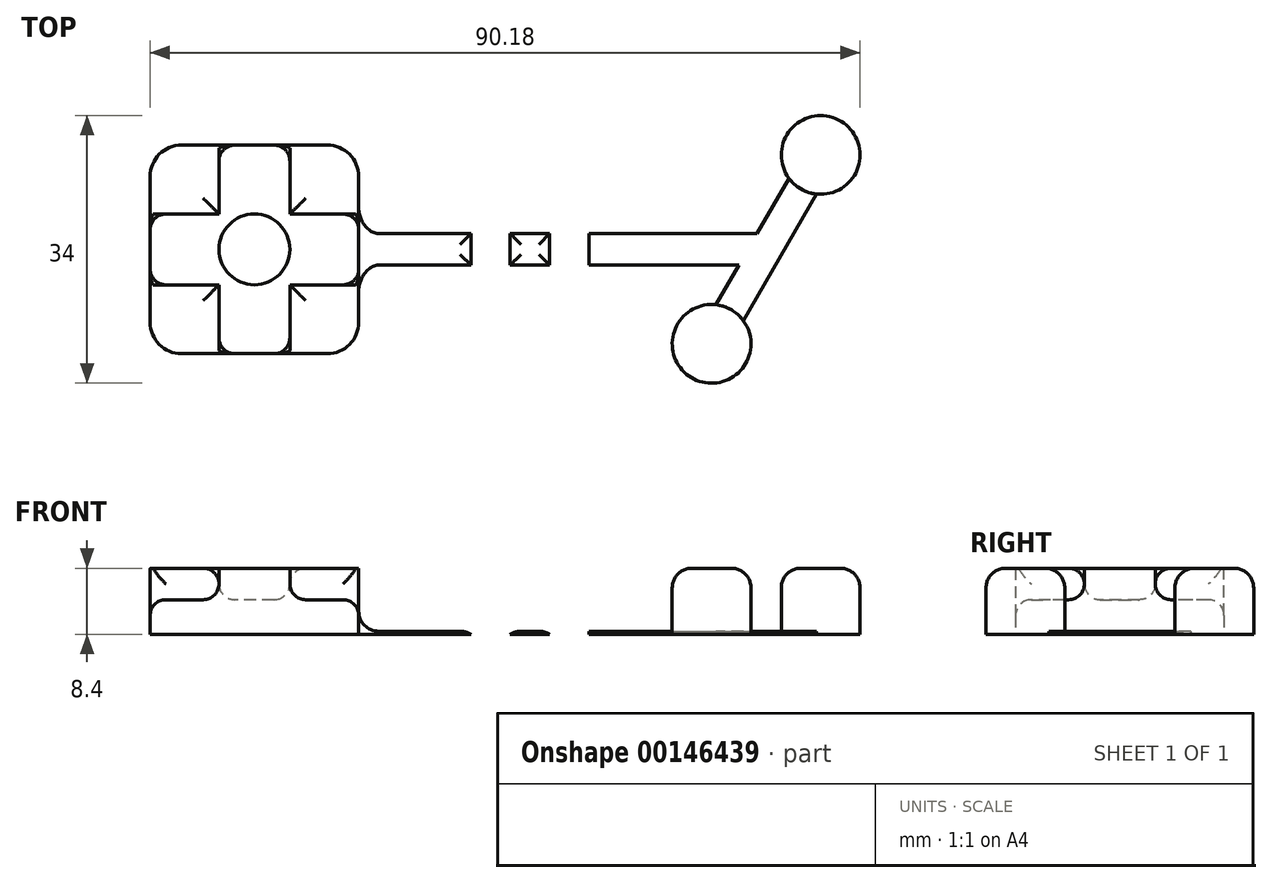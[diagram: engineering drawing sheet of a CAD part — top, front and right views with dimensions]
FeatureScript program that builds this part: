
annotation { "Feature Type Name" : "Feature", "Feature Type Description" : "" }
export const myFeature = defineFeature(function(context is Context, id is Id, definition is map)
    precondition{}
    {
        {
            var Q0;
            Q0=qCreatedBy(makeId("Top.planeOp"),FACE);
            var sketch = newSketch(context, id + "F0", { "sketchPlane" : qUnion([Q0])});
            skLineSegment(sketch, "E0.bottom", {"start": v(13.25, 13.25) * mm, "end": v(-13.25, 13.25) * mm});
            skLineSegment(sketch, "E0.top", {"start": v(13.25, -13.25) * mm, "end": v(-13.25, -13.25) * mm});
            skLineSegment(sketch, "E0.left", {"start": v(13.25, 13.25) * mm, "end": v(13.25, -13.25) * mm});
            skLineSegment(sketch, "E0.right", {"start": v(-13.25, 13.25) * mm, "end": v(-13.25, -13.25) * mm});
            skPoint(sketch, "E0.middle", {"position": v(0, 0) * mm});
            skLineSegment(sketch, "E1", {"start": v(0, 0) * mm, "end": v(65, 0) * mm, "construction": true});
            skLineSegment(sketch, "E2", {"start": v(60.57, -7.67) * mm, "end": v(71.93, 12) * mm, "construction": true});
            skPoint(sketch, "E3", {"position": v(58.07, -12) * mm});
            skCircle(sketch, "E4", {"center": v(71.93, 12) * mm, "radius": 5 * mm});
            skCircle(sketch, "E5", {"center": v(58.07, -12) * mm, "radius": 5 * mm});
            skLineSegment(sketch, "E6.bottom", {"start": v(32.5, 3) * mm, "end": v(27.5, 3) * mm, "construction": true});
            skLineSegment(sketch, "E6.top", {"start": v(32.5, -3) * mm, "end": v(27.5, -3) * mm, "construction": true});
            skLineSegment(sketch, "E6.left", {"start": v(32.5, 3) * mm, "end": v(32.5, -3) * mm});
            skLineSegment(sketch, "E6.right", {"start": v(27.5, 3) * mm, "end": v(27.5, -3) * mm});
            skPoint(sketch, "E6.middle", {"position": v(30, 0) * mm});
            skPoint(sketch, "E7.middle", {"position": v(32.5, 0) * mm});
            skLineSegment(sketch, "E8.bottom", {"start": v(42.5, 3) * mm, "end": v(37.5, 3) * mm, "construction": true});
            skLineSegment(sketch, "E8.top", {"start": v(42.5, -3) * mm, "end": v(37.5, -3) * mm, "construction": true});
            skLineSegment(sketch, "E8.left", {"start": v(42.5, 3) * mm, "end": v(42.5, -3) * mm});
            skLineSegment(sketch, "E8.right", {"start": v(37.5, 3) * mm, "end": v(37.5, -3) * mm});
            skPoint(sketch, "E8.middle", {"position": v(40, 0) * mm});
            skArc(sketch, "E9", {"start": v(37.5, 3) * mm, "mid": v(40, 5.5) * mm, "end": v(42.5, 3) * mm});
            skArc(sketch, "E10", {"start": v(42.5, -3) * mm, "mid": v(40, -5.5) * mm, "end": v(37.5, -3) * mm});
            skArc(sketch, "E11", {"start": v(27.5, 3) * mm, "mid": v(30, 5.5) * mm, "end": v(32.5, 3) * mm});
            skArc(sketch, "E12", {"start": v(32.5, -3) * mm, "mid": v(30, -5.5) * mm, "end": v(27.5, -3) * mm});
            skLineSegment(sketch, "E13.0", {"start": v(58.63, -7.03) * mm, "end": v(67.9, 9.03) * mm});
            skLineSegment(sketch, "E14.MirrorCS", {"start": v(62.1, -9.03) * mm, "end": v(71.37, 7.03) * mm});
            skLineSegment(sketch, "E15", {"start": v(13.25, 2) * mm, "end": v(27.5, 2) * mm});
            skLineSegment(sketch, "E16", {"start": v(32.5, 2) * mm, "end": v(37.5, 2) * mm});
            skLineSegment(sketch, "E17", {"start": v(42.5, 2) * mm, "end": v(63.85, 2) * mm});
            skLineSegment(sketch, "E18.MirrorCS", {"start": v(13.25, -2) * mm, "end": v(27.5, -2) * mm});
            skLineSegment(sketch, "E19.MirrorCS", {"start": v(32.5, -2) * mm, "end": v(37.5, -2) * mm});
            skLineSegment(sketch, "E20.MirrorCS", {"start": v(42.5, -2) * mm, "end": v(63.85, -2) * mm});
            skSolve(sketch);
        }
        {
            var Q0;
            {var subQ3=sQuery(id+"F0.wireOp",EDGE,"E0.bottom");Q0=makeQuery(id+"F0.imprint","IMPRINT",FACE,{"disambiguationData":[TD([[makeQuery(id+"F0.imprint","IMPRINT",EDGE,{"derivedFrom":subQ3}),1.0]])]});}
            var Q1;
            {var subQ0=sQuery(id+"F0.wireOp",EDGE,"E11");Q1=makeQuery(id+"F0.imprint","IMPRINT",FACE,{"disambiguationData":[TD([[makeQuery(id+"F0.imprint","IMPRINT",EDGE,{"derivedFrom":subQ0}),-1.0]])]});}
            var Q2;
            {var subQ0=sQuery(id+"F0.wireOp",EDGE,"E9");Q2=makeQuery(id+"F0.imprint","IMPRINT",FACE,{"disambiguationData":[TD([[makeQuery(id+"F0.imprint","IMPRINT",EDGE,{"derivedFrom":subQ0}),-1.0]])]});}
            var Q3;
            {var subQ0=sQuery(id+"F0.wireOp",EDGE,"E4");var subQ1=makeQuery(id+"F0.imprint","INTERSECT",VERTEX,{"derivedFrom":[subQ0,sQuery(id+"F0.wireOp",EDGE,"E13.0")]});Q3=makeQuery(id+"F0.imprint","IMPRINT",FACE,{"disambiguationData":[TD([[makeQuery(id+"F0.imprint","IMPRINT",EDGE,{"disambiguationData":[TD([[subQ1,-1.0]])],"derivedFrom":subQ0}),1.0]])]});}
            var Q4;
            {var subQ0=sQuery(id+"F0.wireOp",EDGE,"E5");var subQ1=makeQuery(id+"F0.imprint","INTERSECT",VERTEX,{"derivedFrom":[subQ0,sQuery(id+"F0.wireOp",EDGE,"E13.0")]});Q4=makeQuery(id+"F0.imprint","IMPRINT",FACE,{"disambiguationData":[TD([[makeQuery(id+"F0.imprint","IMPRINT",EDGE,{"disambiguationData":[TD([[subQ1,1.0]])],"derivedFrom":subQ0}),1.0]])]});}
            extrude(context, id + "F1", {"entities" : qUnion([Q0, Q1, Q2, Q3, Q4]), "depth" : 8 * mm});
        }
        {
            var Q0;
            {var subQ0=sQuery(id+"F0.wireOp",EDGE,"E15");Q0=makeQuery(id+"F0.imprint","IMPRINT",FACE,{"disambiguationData":[TD([[makeQuery(id+"F0.imprint","IMPRINT",EDGE,{"derivedFrom":subQ0}),-1.0]])]});}
            var Q1;
            {var subQ0=sQuery(id+"F0.wireOp",EDGE,"E16");Q1=makeQuery(id+"F0.imprint","IMPRINT",FACE,{"disambiguationData":[TD([[makeQuery(id+"F0.imprint","IMPRINT",EDGE,{"derivedFrom":subQ0}),-1.0]])]});}
            var Q2;
            {var subQ0=sQuery(id+"F0.wireOp",EDGE,"E17");Q2=makeQuery(id+"F0.imprint","IMPRINT",FACE,{"disambiguationData":[TD([[makeQuery(id+"F0.imprint","IMPRINT",EDGE,{"derivedFrom":subQ0}),-1.0]])]});}
            var Q3;
            {var subQ5=sQuery(id+"F0.wireOp",EDGE,"E14.MirrorCS");Q3=makeQuery(id+"F0.imprint","IMPRINT",FACE,{"disambiguationData":[TD([[makeQuery(id+"F0.imprint","IMPRINT",EDGE,{"derivedFrom":subQ5}),1.0]])]});}
            var Q4;
            Q4=makeQuery(id+"F1.opExtrude","CAP_FACE",FACE,{"disambiguationData":[OSD([sQuery(id+"F0.wireOp",EDGE,"E0.bottom"),sQuery(id+"F0.wireOp",EDGE,"E0.top"),sQuery(id+"F0.wireOp",EDGE,"E0.left"),sQuery(id+"F0.wireOp",EDGE,"E0.right")])],"isStart":false});
            var Q5;
            Q5=makeQuery(id+"F1.opExtrude","CAP_FACE",FACE,{"disambiguationData":[OSD([sQuery(id+"F0.wireOp",EDGE,"E6.left"),sQuery(id+"F0.wireOp",EDGE,"E6.right"),sQuery(id+"F0.wireOp",EDGE,"E11"),sQuery(id+"F0.wireOp",EDGE,"E12")])],"isStart":false});
            var Q6;
            Q6=makeQuery(id+"F1.opExtrude","CAP_FACE",FACE,{"disambiguationData":[OSD([sQuery(id+"F0.wireOp",EDGE,"E8.left"),sQuery(id+"F0.wireOp",EDGE,"E8.right"),sQuery(id+"F0.wireOp",EDGE,"E9"),sQuery(id+"F0.wireOp",EDGE,"E10")])],"isStart":false});
            var Q7;
            Q7=makeQuery(id+"F1.opExtrude","CAP_FACE",FACE,{"disambiguationData":[OSD([sQuery(id+"F0.wireOp",EDGE,"E5")])],"isStart":false});
            var Q8;
            Q8=makeQuery(id+"F1.opExtrude","CAP_FACE",FACE,{"disambiguationData":[OSD([sQuery(id+"F0.wireOp",EDGE,"E4")])],"isStart":false});
            extrude(context, id + "F2", {"entities" : qUnion([Q0, Q1, Q2, Q3, Q4, Q5, Q6, Q7, Q8]), "operationType" : NewBodyOperationType.ADD, "depth" : 0.4 * mm});
        }
        {
            var Q0;
            Q0=makeQuery(id+"F2.opExtrude","CAP_FACE",FACE,{"disambiguationData":[OSD([sQuery(id+"F0.wireOp",EDGE,"E4")])],"isStart":false});
            var Q1;
            Q1=makeQuery(id+"F2.opExtrude","CAP_FACE",FACE,{"disambiguationData":[OSD([sQuery(id+"F0.wireOp",EDGE,"E5")])],"isStart":false});
            var Q2;
            Q2=makeQuery(id+"F2.opExtrude","CAP_FACE",FACE,{"disambiguationData":[OSD([sQuery(id+"F0.wireOp",EDGE,"E8.left"),sQuery(id+"F0.wireOp",EDGE,"E8.right"),sQuery(id+"F0.wireOp",EDGE,"E9"),sQuery(id+"F0.wireOp",EDGE,"E10")])],"isStart":false});
            var Q3;
            Q3=makeQuery(id+"F2.opExtrude","CAP_FACE",FACE,{"disambiguationData":[OSD([sQuery(id+"F0.wireOp",EDGE,"E6.left"),sQuery(id+"F0.wireOp",EDGE,"E6.right"),sQuery(id+"F0.wireOp",EDGE,"E11"),sQuery(id+"F0.wireOp",EDGE,"E12")])],"isStart":false});
            fillet(context, id + "F3", {"entities" : qUnion([Q0, Q1, Q2, Q3]), "radius" : 2.5 * mm, "tangentPropagation" : true, "allowEdgeOverflow" : false});
        }
        {
            var Q0;
            Q0=makeQuery(id+"F2.opExtrude","CAP_FACE",FACE,{"disambiguationData":[OSD([sQuery(id+"F0.wireOp",EDGE,"E0.bottom"),sQuery(id+"F0.wireOp",EDGE,"E0.top"),sQuery(id+"F0.wireOp",EDGE,"E0.left"),sQuery(id+"F0.wireOp",EDGE,"E0.right")])],"isStart":false});
            var sketch = newSketch(context, id + "F4", { "sketchPlane" : qUnion([Q0])});
            skCircle(sketch, "E21", {"center": v(0, 0) * mm, "radius": 4.5 * mm});
            skLineSegment(sketch, "E22", {"start": v(-4.5, 13.25) * mm, "end": v(-4.5, 4.5) * mm});
            skLineSegment(sketch, "E23", {"start": v(-13.25, 4.5) * mm, "end": v(-4.5, 4.5) * mm});
            skLineSegment(sketch, "E24", {"start": v(4.5, 13.25) * mm, "end": v(4.5, 4.5) * mm});
            skLineSegment(sketch, "E25", {"start": v(-13.86, -4.5) * mm, "end": v(-4.5, -4.5) * mm});
            skLineSegment(sketch, "E26.trimOffspring", {"start": v(4.5, 4.5) * mm, "end": v(13.25, 4.5) * mm});
            skLineSegment(sketch, "E27.trimOffspring", {"start": v(4.5, -4.5) * mm, "end": v(13.25, -4.5) * mm});
            skLineSegment(sketch, "E28.trimOffspring", {"start": v(-4.5, -4.5) * mm, "end": v(-4.5, -13.25) * mm});
            skLineSegment(sketch, "E29.trimOffspring", {"start": v(4.5, -4.5) * mm, "end": v(4.5, -13.25) * mm});
            skSolve(sketch);
        }
        {
            var Q0;
            {var subQ0=sQuery(id+"F4.wireOp",EDGE,"E24");Q0=makeQuery(id+"F4.imprint","IMPRINT",FACE,{"disambiguationData":[TD([[makeQuery(id+"F4.imprint","IMPRINT",EDGE,{"derivedFrom":subQ0}),1.0]])]});}
            var Q1;
            {var subQ0=sQuery(id+"F4.wireOp",EDGE,"E22");Q1=makeQuery(id+"F4.imprint","IMPRINT",FACE,{"disambiguationData":[TD([[makeQuery(id+"F4.imprint","IMPRINT",EDGE,{"derivedFrom":subQ0}),-1.0]])]});}
            var Q2;
            {var subQ0=sQuery(id+"F4.wireOp",EDGE,"E28.trimOffspring");Q2=makeQuery(id+"F4.imprint","IMPRINT",FACE,{"disambiguationData":[TD([[makeQuery(id+"F4.imprint","IMPRINT",EDGE,{"derivedFrom":subQ0}),-1.0]])]});}
            var Q3;
            {var subQ0=sQuery(id+"F4.wireOp",EDGE,"E27.trimOffspring");Q3=makeQuery(id+"F4.imprint","IMPRINT",FACE,{"disambiguationData":[TD([[makeQuery(id+"F4.imprint","IMPRINT",EDGE,{"derivedFrom":subQ0}),-1.0]])]});}
            var Q4;
            Q4=makeQuery(id+"F4.imprint","IMPRINT",FACE,{"disambiguationData":[TD([[makeQuery(id+"F4.imprint","IMPRINT",EDGE,{"derivedFrom":sQuery(id+"F4.wireOp",EDGE,"E21")}),1.0]])]});
            extrude(context, id + "F5", {"entities" : qUnion([Q0, Q1, Q2, Q3, Q4]), "operationType" : NewBodyOperationType.REMOVE, "oppositeDirection" : true, "depth" : 4 * mm});
        }
        {
            var Q0;
            Q0=makeQuery(id+"F5.boolean.opBoolean","COPY",FACE,{"derivedFrom":makeQuery(id+"F5.opExtrude","CAP_FACE",FACE,{"disambiguationData":[OSD([sQuery(id+"F0.wireOp",EDGE,"E0.top"),sQuery(id+"F0.wireOp",EDGE,"E0.right"),sQuery(id+"F4.wireOp",EDGE,"E25"),sQuery(id+"F4.wireOp",EDGE,"E28.trimOffspring")])],"isStart":false})});
            var Q1;
            Q1=makeQuery(id+"F5.boolean.opBoolean","COPY",FACE,{"derivedFrom":makeQuery(id+"F5.opExtrude","CAP_FACE",FACE,{"disambiguationData":[OSD([sQuery(id+"F0.wireOp",EDGE,"E0.top"),sQuery(id+"F0.wireOp",EDGE,"E0.left"),sQuery(id+"F4.wireOp",EDGE,"E27.trimOffspring"),sQuery(id+"F4.wireOp",EDGE,"E29.trimOffspring")])],"isStart":false})});
            var Q2;
            Q2=makeQuery(id+"F5.boolean.opBoolean","COPY",FACE,{"derivedFrom":makeQuery(id+"F5.opExtrude","CAP_FACE",FACE,{"disambiguationData":[OSD([sQuery(id+"F0.wireOp",EDGE,"E0.bottom"),sQuery(id+"F0.wireOp",EDGE,"E0.left"),sQuery(id+"F4.wireOp",EDGE,"E24"),sQuery(id+"F4.wireOp",EDGE,"E26.trimOffspring")])],"isStart":false})});
            var Q3;
            Q3=makeQuery(id+"F5.boolean.opBoolean","COPY",FACE,{"derivedFrom":makeQuery(id+"F5.opExtrude","CAP_FACE",FACE,{"disambiguationData":[OSD([sQuery(id+"F0.wireOp",EDGE,"E0.bottom"),sQuery(id+"F0.wireOp",EDGE,"E0.right"),sQuery(id+"F4.wireOp",EDGE,"E22"),sQuery(id+"F4.wireOp",EDGE,"E23")])],"isStart":false})});
            var Q4;
            Q4=makeQuery(id+"F5.boolean.opBoolean","COPY",FACE,{"derivedFrom":makeQuery(id+"F5.opExtrude","SWEPT_FACE",FACE,{"disambiguationData":[OSD([sQuery(id+"F4.wireOp",EDGE,"E21")])]})});
            fillet(context, id + "F6", {"entities" : qUnion([Q0, Q1, Q2, Q3, Q4]), "radius" : 2 * mm, "tangentPropagation" : true, "allowEdgeOverflow" : false});
        }
        {
            var Q0;
            {var subQ0=sQuery(id+"F0.wireOp",EDGE,"E0.right");var subQ1=sQuery(id+"F0.wireOp",EDGE,"E0.top");Q0=makeQuery(id+"F2.boolean.opBoolean","MERGE",EDGE,{"derivedFrom":[makeQuery(id+"F1.opExtrude","SWEPT_EDGE",EDGE,{"disambiguationData":[OSD([subQ1,subQ0])]}),makeQuery(id+"F2.opExtrude","SWEPT_EDGE",EDGE,{"disambiguationData":[OSD([subQ1,subQ0])]})]});}
            var Q1;
            {var subQ0=sQuery(id+"F0.wireOp",EDGE,"E0.left");var subQ1=sQuery(id+"F0.wireOp",EDGE,"E0.top");Q1=makeQuery(id+"F2.boolean.opBoolean","MERGE",EDGE,{"derivedFrom":[makeQuery(id+"F1.opExtrude","SWEPT_EDGE",EDGE,{"disambiguationData":[OSD([subQ1,subQ0])]}),makeQuery(id+"F2.opExtrude","SWEPT_EDGE",EDGE,{"disambiguationData":[OSD([subQ1,subQ0])]})]});}
            var Q2;
            {var subQ0=sQuery(id+"F0.wireOp",EDGE,"E0.left");var subQ1=sQuery(id+"F0.wireOp",EDGE,"E0.bottom");Q2=makeQuery(id+"F2.boolean.opBoolean","MERGE",EDGE,{"derivedFrom":[makeQuery(id+"F1.opExtrude","SWEPT_EDGE",EDGE,{"disambiguationData":[OSD([subQ1,subQ0])]}),makeQuery(id+"F2.opExtrude","SWEPT_EDGE",EDGE,{"disambiguationData":[OSD([subQ1,subQ0])]})]});}
            var Q3;
            {var subQ0=sQuery(id+"F0.wireOp",EDGE,"E0.right");var subQ1=sQuery(id+"F0.wireOp",EDGE,"E0.bottom");Q3=makeQuery(id+"F2.boolean.opBoolean","MERGE",EDGE,{"derivedFrom":[makeQuery(id+"F1.opExtrude","SWEPT_EDGE",EDGE,{"disambiguationData":[OSD([subQ1,subQ0])]}),makeQuery(id+"F2.opExtrude","SWEPT_EDGE",EDGE,{"disambiguationData":[OSD([subQ1,subQ0])]})]});}
            fillet(context, id + "F7", {"entities" : qUnion([Q0, Q1, Q2, Q3]), "radius" : 4 * mm, "tangentPropagation" : true, "allowEdgeOverflow" : false});
        }
    });
